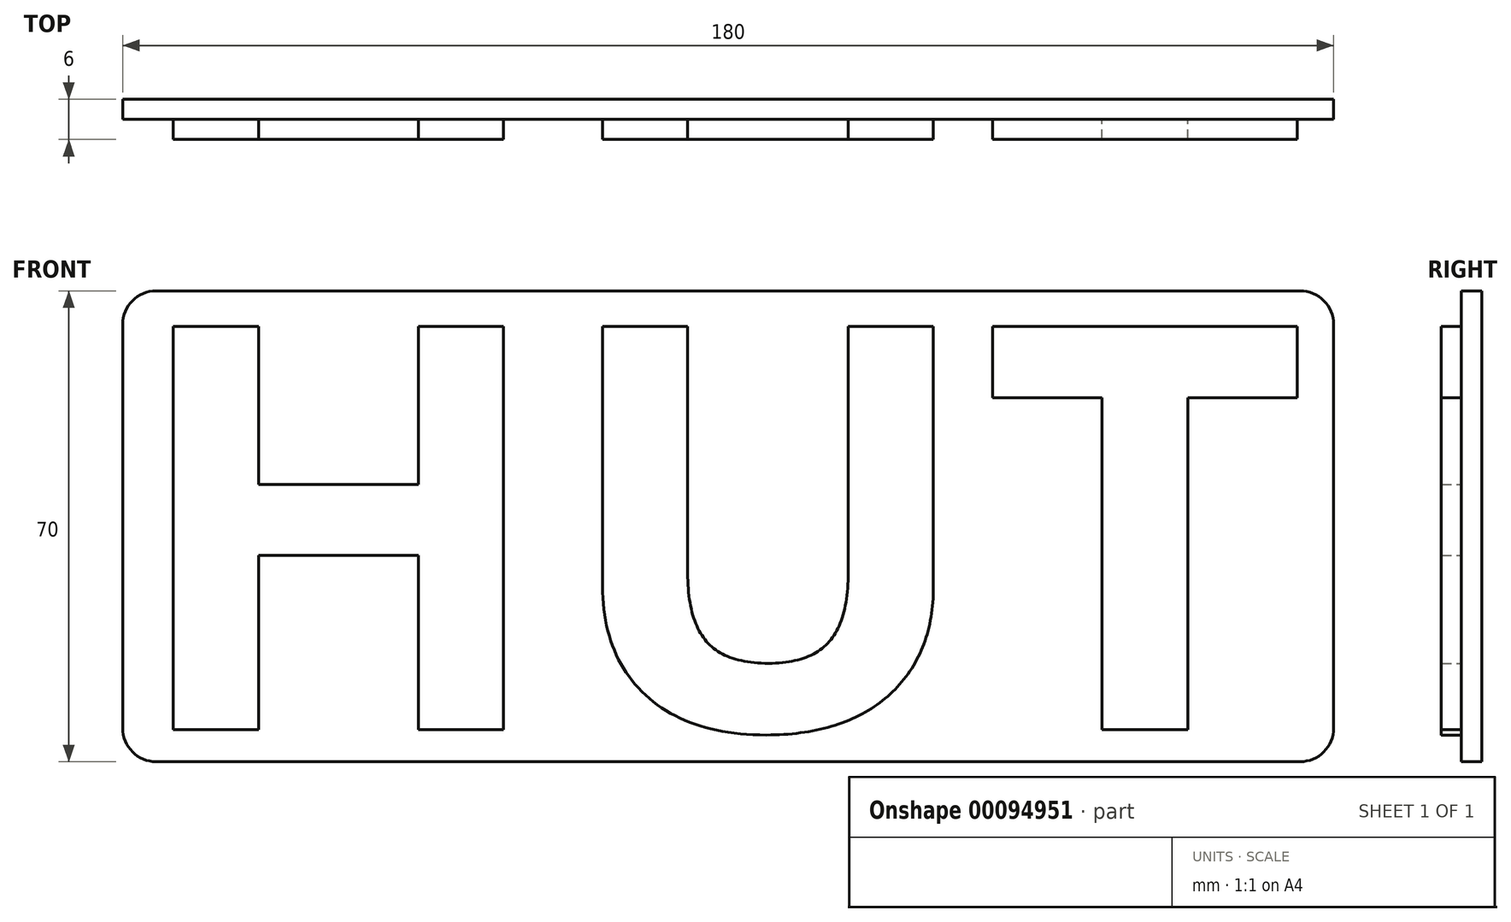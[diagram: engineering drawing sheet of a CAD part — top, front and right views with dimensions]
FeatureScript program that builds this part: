
annotation { "Feature Type Name" : "Feature", "Feature Type Description" : "" }
export const myFeature = defineFeature(function(context is Context, id is Id, definition is map)
    precondition{}
    {
        {
            var Q0;
            Q0=qCreatedBy(makeId("Front.planeOp"),FACE);
            var sketch = newSketch(context, id + "F0", { "sketchPlane" : qUnion([Q0])});
            skText(sketch, "E0", { "text": "HUT", "fontName": "OpenSans-Bold.ttf"});
            skLineSegment(sketch, "E1.bottom", {"start": v(116.35, 46.1) * mm, "end": v(-63.65, 46.1) * mm});
            skLineSegment(sketch, "E1.top", {"start": v(116.35, -23.9) * mm, "end": v(-63.65, -23.9) * mm});
            skLineSegment(sketch, "E1.left", {"start": v(116.35, 46.1) * mm, "end": v(116.35, -23.9) * mm});
            skLineSegment(sketch, "E1.right", {"start": v(-63.65, 46.1) * mm, "end": v(-63.65, -23.9) * mm});
            skPoint(sketch, "E1.middle", {"position": v(26.35, 11.1) * mm});
            const initialGuessF0  = {"E0": [-0.06365, -0.0191, 1, 0, 0.06042]};
            skSetInitialGuess(sketch, initialGuessF0);
            skSolve(sketch);
        }
        {
            var Q0;
            Q0=makeQuery(id+"F0.imprint","IMPRINT",FACE,{"disambiguationData":[TD([[makeQuery(id+"F0.imprint","IMPRINT",EDGE,{"derivedFrom":sQuery(id+"F0.wireOp",EDGE,"E0.sketch_text.stroke-0")}),-1.0]])]});
            extrude(context, id + "F1", {"entities" : qUnion([Q0]), "depth" : 6 * mm});
        }
        {
            var Q0;
            Q0=makeQuery(id+"F0.imprint","IMPRINT",FACE,{"disambiguationData":[TD([[makeQuery(id+"F0.imprint","IMPRINT",EDGE,{"derivedFrom":sQuery(id+"F0.wireOp",EDGE,"E0.sketch_text.stroke-0")}),1.0]])]});
            extrude(context, id + "F2", {"entities" : qUnion([Q0]), "operationType" : NewBodyOperationType.ADD, "depth" : 3 * mm});
        }
        {
            var Q0;
            Q0=makeQuery(id+"F0.imprint","IMPRINT",FACE,{"disambiguationData":[TD([[makeQuery(id+"F0.imprint","IMPRINT",EDGE,{"derivedFrom":sQuery(id+"F0.wireOp",EDGE,"E0.sketch_text.stroke-12")}),-1.0]])]});
            extrude(context, id + "F3", {"entities" : qUnion([Q0]), "operationType" : NewBodyOperationType.ADD, "depth" : 6 * mm});
        }
        {
            var Q0;
            Q0=makeQuery(id+"F0.imprint","IMPRINT",FACE,{"disambiguationData":[TD([[makeQuery(id+"F0.imprint","IMPRINT",EDGE,{"derivedFrom":sQuery(id+"F0.wireOp",EDGE,"E0.sketch_text.stroke-27")}),-1.0]])]});
            extrude(context, id + "F4", {"entities" : qUnion([Q0]), "operationType" : NewBodyOperationType.ADD, "depth" : 6 * mm});
        }
        {
            var Q0;
            Q0=makeQuery(id+"F2.opExtrude","SWEPT_EDGE",EDGE,{"disambiguationData":[OSD([sQuery(id+"F0.wireOp",EDGE,"E1.bottom"),sQuery(id+"F0.wireOp",EDGE,"E1.right")])]});
            var Q1;
            Q1=makeQuery(id+"F2.opExtrude","SWEPT_EDGE",EDGE,{"disambiguationData":[OSD([sQuery(id+"F0.wireOp",EDGE,"E1.bottom"),sQuery(id+"F0.wireOp",EDGE,"E1.left")])]});
            var Q2;
            Q2=makeQuery(id+"F2.opExtrude","SWEPT_EDGE",EDGE,{"disambiguationData":[OSD([sQuery(id+"F0.wireOp",EDGE,"E1.top"),sQuery(id+"F0.wireOp",EDGE,"E1.right")])]});
            var Q3;
            Q3=makeQuery(id+"F2.opExtrude","SWEPT_EDGE",EDGE,{"disambiguationData":[OSD([sQuery(id+"F0.wireOp",EDGE,"E1.top"),sQuery(id+"F0.wireOp",EDGE,"E1.left")])]});
            fillet(context, id + "F5", {"entities" : qUnion([Q0, Q1, Q2, Q3]), "radius" : 5 * mm, "tangentPropagation" : true, "allowEdgeOverflow" : false});
        }
    });
